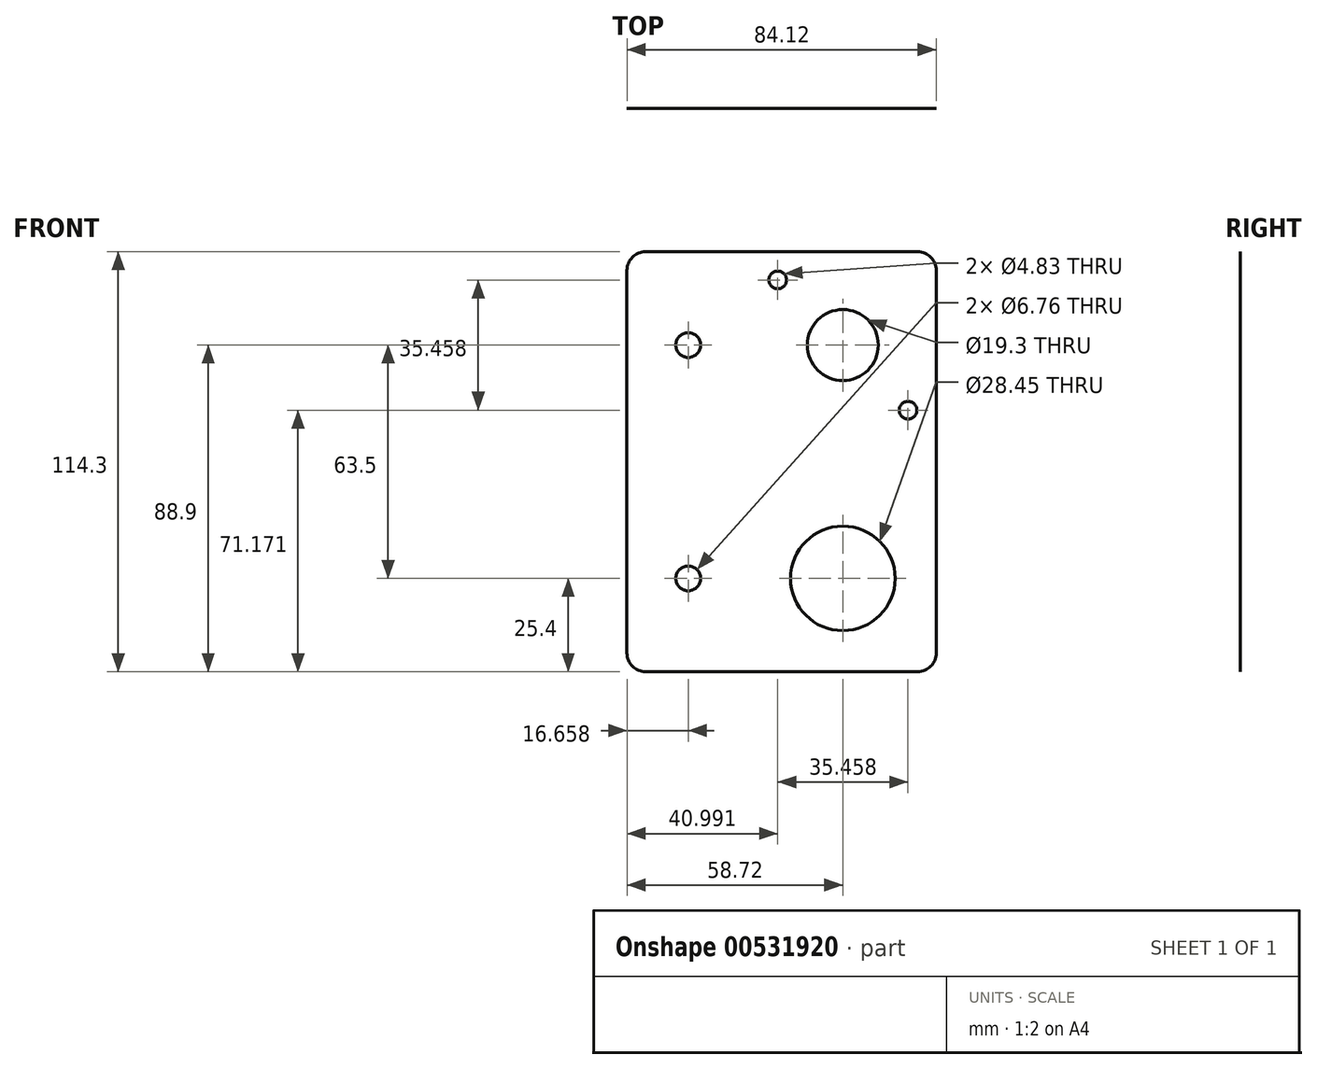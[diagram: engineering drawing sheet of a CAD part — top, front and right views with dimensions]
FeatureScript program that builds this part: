
annotation { "Feature Type Name" : "Feature", "Feature Type Description" : "" }
export const myFeature = defineFeature(function(context is Context, id is Id, definition is map)
    precondition{}
    {
        {
            var Q0;
            Q0=qCreatedBy(makeId("Front.planeOp"),FACE);
            var sketch = newSketch(context, id + "F0", { "sketchPlane" : qUnion([Q0])});
            skCircle(sketch, "E0", {"center": v(0, 0) * mm, "radius": 9.65 * mm});
            skLineSegment(sketch, "E1.bottom", {"start": v(17.73, -17.73) * mm, "end": v(-17.73, -17.73) * mm, "construction": true});
            skLineSegment(sketch, "E1.top", {"start": v(17.73, 17.73) * mm, "end": v(-17.73, 17.73) * mm, "construction": true});
            skLineSegment(sketch, "E1.left", {"start": v(17.73, -17.73) * mm, "end": v(17.73, 17.73) * mm, "construction": true});
            skLineSegment(sketch, "E1.right", {"start": v(-17.73, -17.73) * mm, "end": v(-17.73, 17.73) * mm, "construction": true});
            skCircle(sketch, "E2", {"center": v(-17.73, 17.73) * mm, "radius": 2.41 * mm});
            skCircle(sketch, "E3", {"center": v(17.73, -17.73) * mm, "radius": 2.41 * mm});
            skLineSegment(sketch, "E4", {"start": v(0, 0) * mm, "end": v(0, -63.5) * mm, "construction": true});
            skCircle(sketch, "E5", {"center": v(0, -63.5) * mm, "radius": 14.22 * mm});
            skPoint(sketch, "E6", {"position": v(0, -31.75) * mm});
            skLineSegment(sketch, "E7.bottom", {"start": v(25.4, -88.9) * mm, "end": v(-25.4, -88.9) * mm});
            skLineSegment(sketch, "E7.top", {"start": v(25.4, 25.4) * mm, "end": v(-25.4, 25.4) * mm});
            skLineSegment(sketch, "E7.left", {"start": v(25.4, -88.9) * mm, "end": v(25.4, 25.4) * mm});
            skLineSegment(sketch, "E8.bottom", {"start": v(-25.4, 25.4) * mm, "end": v(-58.72, 25.4) * mm});
            skLineSegment(sketch, "E8.top", {"start": v(-25.4, -88.9) * mm, "end": v(-58.72, -88.9) * mm});
            skLineSegment(sketch, "E8.right", {"start": v(-58.72, 25.4) * mm, "end": v(-58.72, -88.9) * mm});
            skPoint(sketch, "E9", {"position": v(-42.06, 25.4) * mm});
            skLineSegment(sketch, "E10", {"start": v(-42.06, 25.4) * mm, "end": v(-42.06, -88.9) * mm, "construction": true});
            skLineSegment(sketch, "E11", {"start": v(0, -63.5) * mm, "end": v(-58.72, -63.5) * mm, "construction": true});
            skLineSegment(sketch, "E12", {"start": v(0, 0) * mm, "end": v(-58.72, 0) * mm, "construction": true});
            skCircle(sketch, "E13", {"center": v(-42.06, -63.5) * mm, "radius": 3.38 * mm});
            skCircle(sketch, "E14", {"center": v(0, -63.5) * mm, "radius": 31.75 * mm, "construction": true});
            skCircle(sketch, "E15", {"center": v(0, 0) * mm, "radius": 31.75 * mm, "construction": true});
            skCircle(sketch, "E16", {"center": v(-42.06, 0) * mm, "radius": 3.38 * mm});
            skSolve(sketch);
        }
        {
            var Q0;
            Q0=makeQuery(id+"F0.imprint","IMPRINT",FACE,{"disambiguationData":[TD([[makeQuery(id+"F0.imprint","IMPRINT",EDGE,{"derivedFrom":sQuery(id+"F0.wireOp",EDGE,"E0")}),-1.0]])]});
            extrude(context, id + "F1", {"entities" : qUnion([Q0]), "depth" : 1 / 203.2 * mm, "offsetDistance" : 25.4 * mm});
        }
        {
            var Q0;
            Q0=makeQuery(id+"F1.opExtrude","SWEPT_EDGE",EDGE,{"disambiguationData":[OSD([sQuery(id+"F0.wireOp",EDGE,"E7.bottom"),sQuery(id+"F0.wireOp",EDGE,"E7.right")])]});
            var Q1;
            Q1=makeQuery(id+"F1.opExtrude","SWEPT_EDGE",EDGE,{"disambiguationData":[OSD([sQuery(id+"F0.wireOp",EDGE,"E7.bottom"),sQuery(id+"F0.wireOp",EDGE,"E7.left")])]});
            var Q2;
            Q2=makeQuery(id+"F1.opExtrude","SWEPT_EDGE",EDGE,{"disambiguationData":[OSD([sQuery(id+"F0.wireOp",EDGE,"E7.top"),sQuery(id+"F0.wireOp",EDGE,"E7.left")])]});
            var Q3;
            Q3=makeQuery(id+"F1.opExtrude","SWEPT_EDGE",EDGE,{"disambiguationData":[OSD([sQuery(id+"F0.wireOp",EDGE,"E7.top"),sQuery(id+"F0.wireOp",EDGE,"E7.right")])]});
            fillet(context, id + "F2", {"entities" : qUnion([Q0, Q1, Q2, Q3]), "radius" : 5.08 * mm, "tangentPropagation" : true, "allowEdgeOverflow" : false});
        }
        {
            var Q0;
            Q0=makeQuery(id+"F1.opExtrude","SWEPT_EDGE",EDGE,{"disambiguationData":[OSD([sQuery(id+"F0.wireOp",EDGE,"E8.bottom"),sQuery(id+"F0.wireOp",EDGE,"E8.right")])]});
            var Q1;
            Q1=makeQuery(id+"F1.opExtrude","SWEPT_EDGE",EDGE,{"disambiguationData":[OSD([sQuery(id+"F0.wireOp",EDGE,"E8.top"),sQuery(id+"F0.wireOp",EDGE,"E8.right")])]});
            fillet(context, id + "F3", {"entities" : qUnion([Q0, Q1]), "radius" : 5.08 * mm, "tangentPropagation" : true, "allowEdgeOverflow" : false});
        }
    });
